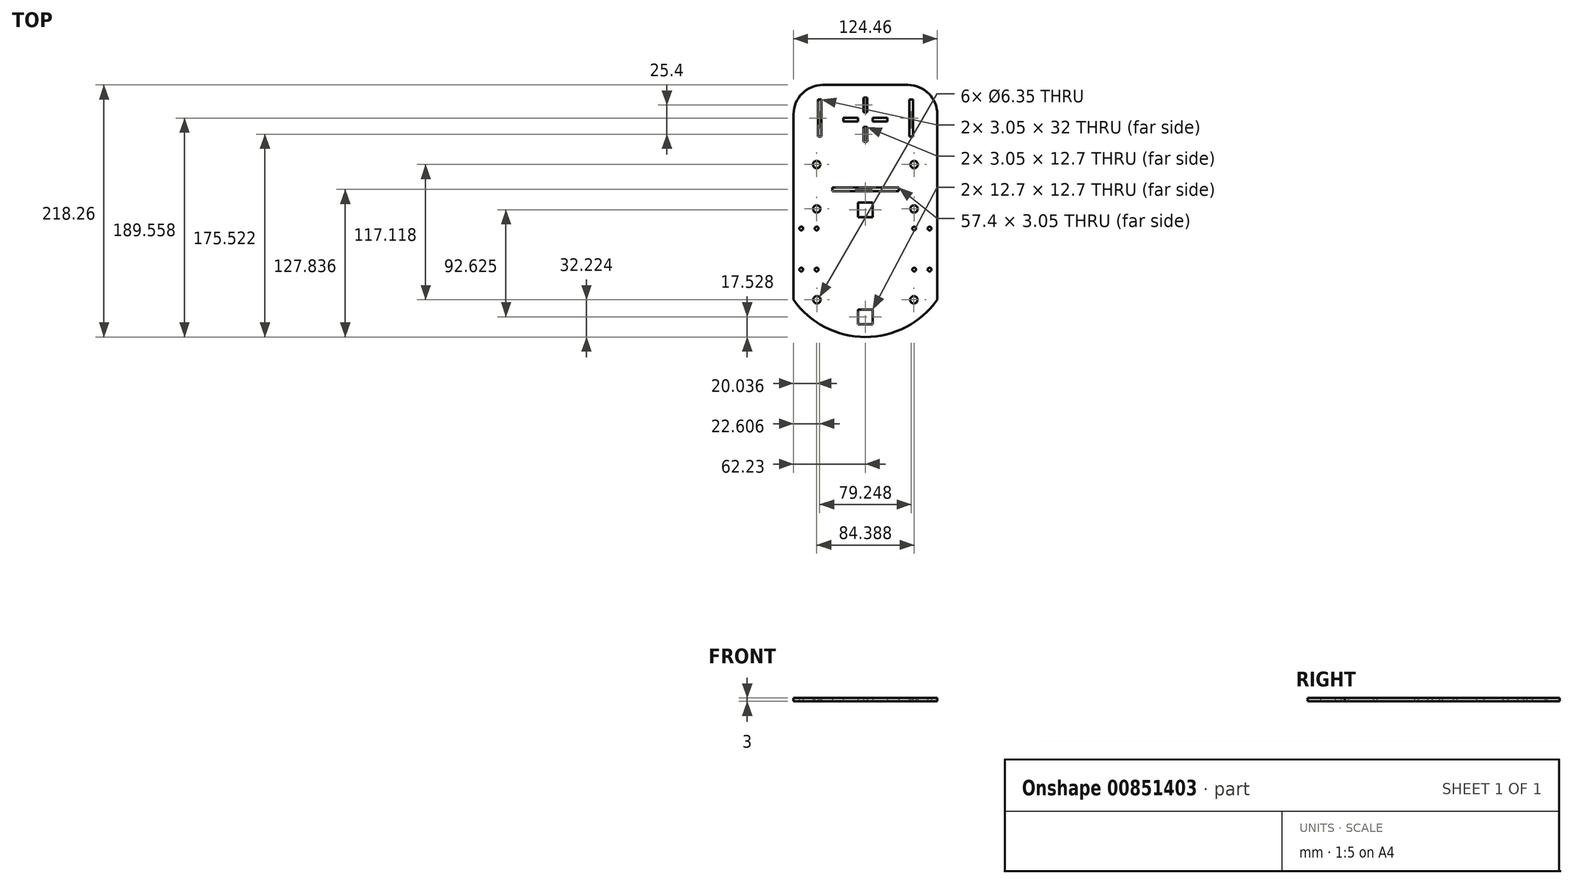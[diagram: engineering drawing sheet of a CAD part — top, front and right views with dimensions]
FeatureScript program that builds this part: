
annotation { "Feature Type Name" : "Feature", "Feature Type Description" : "" }
export const myFeature = defineFeature(function(context is Context, id is Id, definition is map)
    precondition{}
    {
        {
            var Q0;
            Q0=qCreatedBy(makeId("Top.planeOp"),FACE);
            var sketch = newSketch(context, id + "F0", { "sketchPlane" : qUnion([Q0])});
            skArc(sketch, "E0", {"start": v(-62.23, -43.98) * mm, "mid": v(0, -76.2) * mm, "end": v(62.23, -43.98) * mm});
            skLineSegment(sketch, "E1", {"start": v(-62.23, 43.98) * mm, "end": v(-62.23, -43.98) * mm});
            skLineSegment(sketch, "E2.MirrorCS", {"start": v(62.23, 43.98) * mm, "end": v(62.23, -43.98) * mm});
            skCircle(sketch, "E3", {"center": v(-55.55, 17.78) * mm, "radius": 1.59 * mm});
            skCircle(sketch, "E4", {"center": v(-42.21, 17.78) * mm, "radius": 1.59 * mm});
            skCircle(sketch, "E5", {"center": v(-55.55, -17.78) * mm, "radius": 1.59 * mm});
            skCircle(sketch, "E6", {"center": v(-42.21, -17.78) * mm, "radius": 1.59 * mm});
            skCircle(sketch, "E7.MirrorC", {"center": v(42.21, -17.78) * mm, "radius": 1.59 * mm});
            skCircle(sketch, "E8.MirrorC", {"center": v(55.55, -17.78) * mm, "radius": 1.59 * mm});
            skCircle(sketch, "E9.MirrorC", {"center": v(42.21, 17.78) * mm, "radius": 1.59 * mm});
            skCircle(sketch, "E10.MirrorC", {"center": v(55.55, 17.78) * mm, "radius": 1.59 * mm});
            skLineSegment(sketch, "E11", {"start": v(0, 0) * mm, "end": v(0, 112.02) * mm, "construction": true});
            skLineSegment(sketch, "E12", {"start": v(0, 112.02) * mm, "end": v(0, -105.16) * mm, "construction": true});
            skLineSegment(sketch, "E13.bottom", {"start": v(-36.83, 142.06) * mm, "end": v(36.83, 142.06) * mm});
            skLineSegment(sketch, "E13.left", {"start": v(-62.23, 116.66) * mm, "end": v(-62.23, 67.2) * mm});
            skLineSegment(sketch, "E13.right", {"start": v(62.23, 116.66) * mm, "end": v(62.23, 67.24) * mm});
            skPoint(sketch, "E14.visualSharp", {"position": v(-62.23, 142.06) * mm});
            skArc(sketch, "E14.filletArc", {"start": v(-36.83, 142.06) * mm, "mid": v(-54.8, 134.62) * mm, "end": v(-62.23, 116.66) * mm});
            skPoint(sketch, "E15.visualSharp", {"position": v(62.23, 142.06) * mm});
            skArc(sketch, "E15.filletArc", {"start": v(62.23, 116.66) * mm, "mid": v(54.8, 134.62) * mm, "end": v(36.83, 142.06) * mm});
            skLineSegment(sketch, "E16", {"start": v(-36.83, 116.66) * mm, "end": v(-36.83, 129.17) * mm, "construction": true});
            skLineSegment(sketch, "E17", {"start": v(-36.83, 129.17) * mm, "end": v(-36.83, 97.14) * mm, "construction": true});
            skLineSegment(sketch, "E18.bottom", {"start": v(-41.15, 129.36) * mm, "end": v(-38.1, 129.36) * mm});
            skLineSegment(sketch, "E18.top", {"start": v(-41.15, 97.36) * mm, "end": v(-38.1, 97.36) * mm});
            skLineSegment(sketch, "E18.left", {"start": v(-41.15, 129.36) * mm, "end": v(-41.15, 97.36) * mm});
            skLineSegment(sketch, "E18.right", {"start": v(-38.1, 129.36) * mm, "end": v(-38.1, 97.36) * mm});
            skLineSegment(sketch, "E19.MirrorCS", {"start": v(41.15, 129.36) * mm, "end": v(38.1, 129.36) * mm});
            skLineSegment(sketch, "E20.MirrorCS", {"start": v(41.15, 97.36) * mm, "end": v(38.1, 97.36) * mm});
            skLineSegment(sketch, "E21.MirrorCS", {"start": v(38.1, 129.36) * mm, "end": v(38.1, 97.36) * mm});
            skLineSegment(sketch, "E22.MirrorCS", {"start": v(36.83, 116.66) * mm, "end": v(36.83, 129.17) * mm, "construction": true});
            skLineSegment(sketch, "E23.MirrorCS", {"start": v(41.15, 129.36) * mm, "end": v(41.15, 97.36) * mm});
            skLineSegment(sketch, "E24.MirrorCS", {"start": v(36.83, 129.17) * mm, "end": v(36.83, 97.14) * mm, "construction": true});
            skLineSegment(sketch, "E25.bottom", {"start": v(-28.7, 53.16) * mm, "end": v(28.7, 53.16) * mm});
            skLineSegment(sketch, "E25.top", {"start": v(-28.7, 50.11) * mm, "end": v(28.7, 50.11) * mm});
            skLineSegment(sketch, "E25.left", {"start": v(-28.7, 53.16) * mm, "end": v(-28.7, 50.11) * mm});
            skLineSegment(sketch, "E25.right", {"start": v(28.7, 53.16) * mm, "end": v(28.7, 50.11) * mm});
            skLineSegment(sketch, "E26", {"start": v(62.23, 67.24) * mm, "end": v(62.23, 43.98) * mm});
            skLineSegment(sketch, "E27", {"start": v(-62.23, 43.98) * mm, "end": v(-62.23, 67.2) * mm});
            skCircle(sketch, "E28", {"center": v(0, 112.02) * mm, "radius": 25.4 * mm, "construction": true});
            skCircle(sketch, "E29", {"center": v(0, 112.02) * mm, "radius": 22.23 * mm, "construction": true});
            skLineSegment(sketch, "E30", {"start": v(-25.4, 112.02) * mm, "end": v(25.4, 112.02) * mm, "construction": true});
            skLineSegment(sketch, "E31", {"start": v(0, 112.02) * mm, "end": v(0, 137.42) * mm, "construction": true});
            skLineSegment(sketch, "E32.bottom", {"start": v(-19.05, 113.55) * mm, "end": v(-6.35, 113.55) * mm});
            skLineSegment(sketch, "E32.top", {"start": v(-19.05, 110.5) * mm, "end": v(-6.35, 110.5) * mm});
            skLineSegment(sketch, "E32.left", {"start": v(-19.05, 113.55) * mm, "end": v(-19.05, 110.5) * mm});
            skLineSegment(sketch, "E32.right", {"start": v(-6.35, 113.55) * mm, "end": v(-6.35, 110.5) * mm});
            skLineSegment(sketch, "E33.MirrorCS", {"start": v(19.05, 110.5) * mm, "end": v(6.35, 110.5) * mm});
            skLineSegment(sketch, "E34.MirrorCS", {"start": v(19.05, 113.55) * mm, "end": v(19.05, 110.5) * mm});
            skLineSegment(sketch, "E35.MirrorCS", {"start": v(19.05, 113.55) * mm, "end": v(6.35, 113.55) * mm});
            skLineSegment(sketch, "E36.MirrorCS", {"start": v(6.35, 113.55) * mm, "end": v(6.35, 110.5) * mm});
            skLineSegment(sketch, "E37.bottom", {"start": v(-1.52, 131.07) * mm, "end": v(1.52, 131.07) * mm});
            skLineSegment(sketch, "E37.top", {"start": v(-1.52, 118.37) * mm, "end": v(1.52, 118.37) * mm});
            skLineSegment(sketch, "E37.left", {"start": v(-1.52, 131.07) * mm, "end": v(-1.52, 118.37) * mm});
            skLineSegment(sketch, "E37.right", {"start": v(1.52, 131.07) * mm, "end": v(1.52, 118.37) * mm});
            skLineSegment(sketch, "E38.MirrorCS", {"start": v(-1.52, 105.67) * mm, "end": v(1.52, 105.67) * mm});
            skLineSegment(sketch, "E39.MirrorCS", {"start": v(-1.52, 92.97) * mm, "end": v(-1.52, 105.67) * mm});
            skLineSegment(sketch, "E40.MirrorCS", {"start": v(-1.52, 92.97) * mm, "end": v(1.52, 92.97) * mm});
            skLineSegment(sketch, "E41.MirrorCS", {"start": v(1.52, 92.97) * mm, "end": v(1.52, 105.67) * mm});
            skLineSegment(sketch, "E42.bottom", {"start": v(-6.35, 40.3) * mm, "end": v(6.35, 40.3) * mm});
            skLineSegment(sketch, "E42.top", {"start": v(-6.35, 27.6) * mm, "end": v(6.35, 27.6) * mm});
            skLineSegment(sketch, "E42.left", {"start": v(-6.35, 40.3) * mm, "end": v(-6.35, 27.6) * mm});
            skLineSegment(sketch, "E42.right", {"start": v(6.35, 40.3) * mm, "end": v(6.35, 27.6) * mm});
            skLineSegment(sketch, "E43.bottom", {"start": v(-6.35, -52.32) * mm, "end": v(6.35, -52.32) * mm});
            skLineSegment(sketch, "E43.top", {"start": v(-6.35, -65.02) * mm, "end": v(6.35, -65.02) * mm});
            skLineSegment(sketch, "E43.left", {"start": v(-6.35, -52.32) * mm, "end": v(-6.35, -65.02) * mm});
            skLineSegment(sketch, "E43.right", {"start": v(6.35, -52.32) * mm, "end": v(6.35, -65.02) * mm});
            skCircle(sketch, "E44", {"center": v(41.96, -43.98) * mm, "radius": 3.18 * mm});
            skCircle(sketch, "E45.MirrorC", {"center": v(-41.96, -43.98) * mm, "radius": 3.18 * mm});
            skLineSegment(sketch, "E46", {"start": v(41.96, -43.98) * mm, "end": v(62.23, -43.98) * mm, "construction": true});
            skLineSegment(sketch, "E47", {"start": v(41.96, -43.98) * mm, "end": v(42.21, 83.67) * mm, "construction": true});
            skCircle(sketch, "E48", {"center": v(42.12, 34.73) * mm, "radius": 3.18 * mm});
            skCircle(sketch, "E49", {"center": v(42.2, 73.14) * mm, "radius": 3.18 * mm});
            skCircle(sketch, "E50.MirrorC", {"center": v(-42.12, 34.73) * mm, "radius": 3.18 * mm});
            skCircle(sketch, "E51.MirrorC", {"center": v(-42.2, 73.14) * mm, "radius": 3.18 * mm});
            skSolve(sketch);
        }
        {
            var Q0;
            Q0=qSketchRegion(id+"F0",true);
            extrude(context, id + "F1", {"entities" : qUnion([Q0]), "depth" : 3 * mm, "offsetDistance" : 25.4 * mm});
        }
    });
